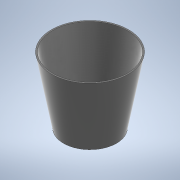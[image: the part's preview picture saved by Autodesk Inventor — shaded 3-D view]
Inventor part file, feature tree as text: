
AUTODESK INVENTOR PART (.ipt)
format: ipt  version: 2020 (Build 240168000, 168)  size: 115,712 bytes
history: native  units: in
note: dims shown in document units (in); Inventor stores cm internally (conversion verified against a paired STEP export)
features: revolve x1, shell x1, sketch x1
ambient origin geometry x8: Origin, YZ Plane, XZ Plane, XY Plane, X Axis, Y Axis, Z Axis, Center Point
bodies: Solid1 (feature_tree)
feature tree (3):
  revolve  "Revolution1"  [1 undecoded]
  shell  "Shell1"  Thickness=0.875in
  sketch  "Sketch1"  dims[d0=0.6in d1=1.5in d2=0.875in d3=90.0deg d4=0.03in]
note: 1 required parameter value undecoded (feature->parameter linkage not recoverable at this tier; creation-order binding heuristic only, values carry confidence <= 0.55)
